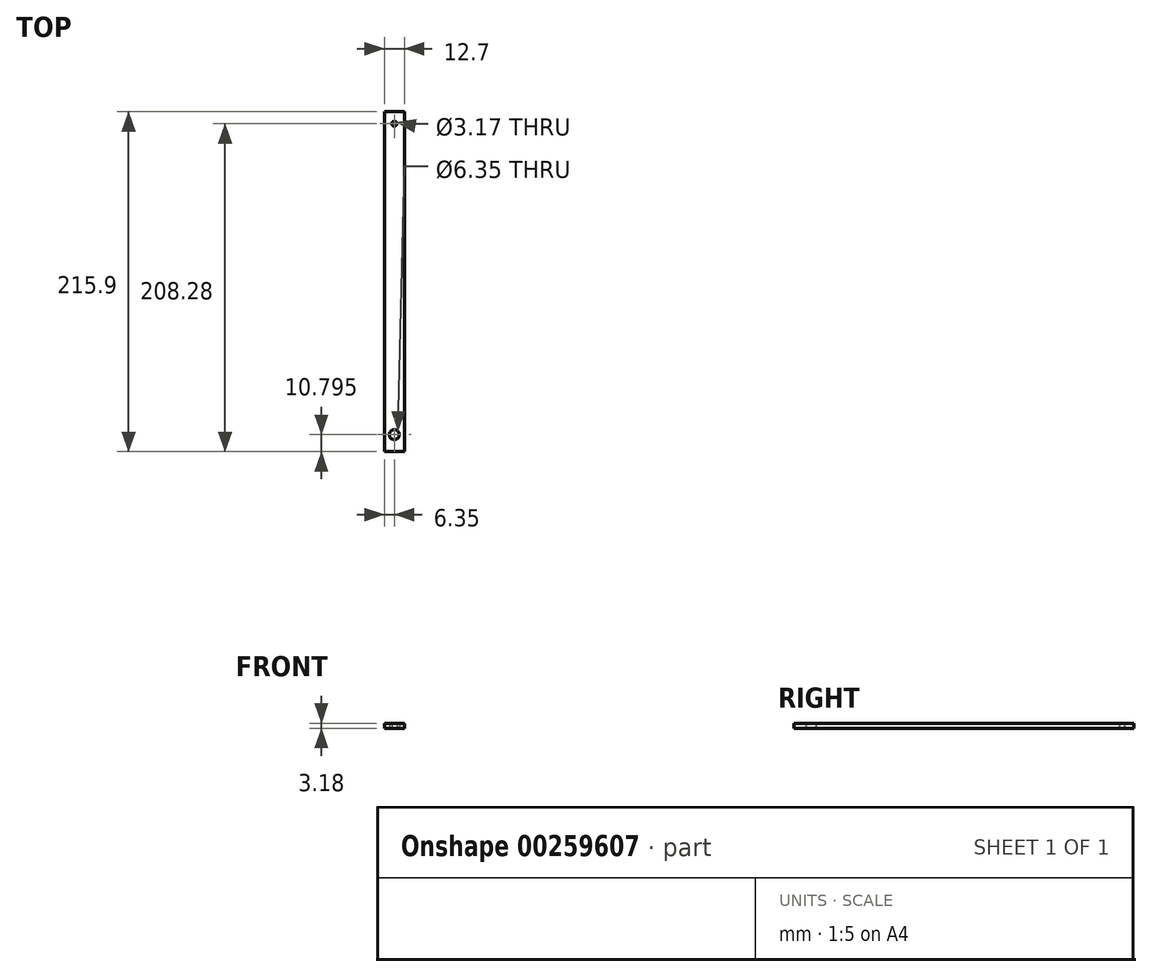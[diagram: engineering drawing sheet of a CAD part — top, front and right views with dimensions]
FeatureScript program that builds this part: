
annotation { "Feature Type Name" : "Feature", "Feature Type Description" : "" }
export const myFeature = defineFeature(function(context is Context, id is Id, definition is map)
    precondition{}
    {
        {
            var Q0;
            Q0=qCreatedBy(makeId("Top.planeOp"),FACE);
            var sketch = newSketch(context, id + "F0", { "sketchPlane" : qUnion([Q0])});
            skLineSegment(sketch, "E0.bottom", {"start": v(6.35, -107.95) * mm, "end": v(-6.35, -107.95) * mm});
            skLineSegment(sketch, "E0.top", {"start": v(6.35, 107.95) * mm, "end": v(-6.35, 107.95) * mm});
            skLineSegment(sketch, "E0.left", {"start": v(6.35, -107.95) * mm, "end": v(6.35, 107.95) * mm});
            skLineSegment(sketch, "E0.right", {"start": v(-6.35, -107.95) * mm, "end": v(-6.35, 107.95) * mm});
            skPoint(sketch, "E0.middle", {"position": v(0, 0) * mm});
            skCircle(sketch, "E1", {"center": v(0, 100.33) * mm, "radius": 1.59 * mm});
            skCircle(sketch, "E2", {"center": v(0, -97.16) * mm, "radius": 3.18 * mm});
            skSolve(sketch);
        }
        {
            var Q0;
            Q0=makeQuery(id+"F0.imprint","IMPRINT",FACE,{"disambiguationData":[TD([[makeQuery(id+"F0.imprint","IMPRINT",EDGE,{"derivedFrom":sQuery(id+"F0.wireOp",EDGE,"E0.bottom")}),-1.0]])]});
            extrude(context, id + "F1", {"entities" : qUnion([Q0]), "depth" : 3.17 * mm});
        }
    });
